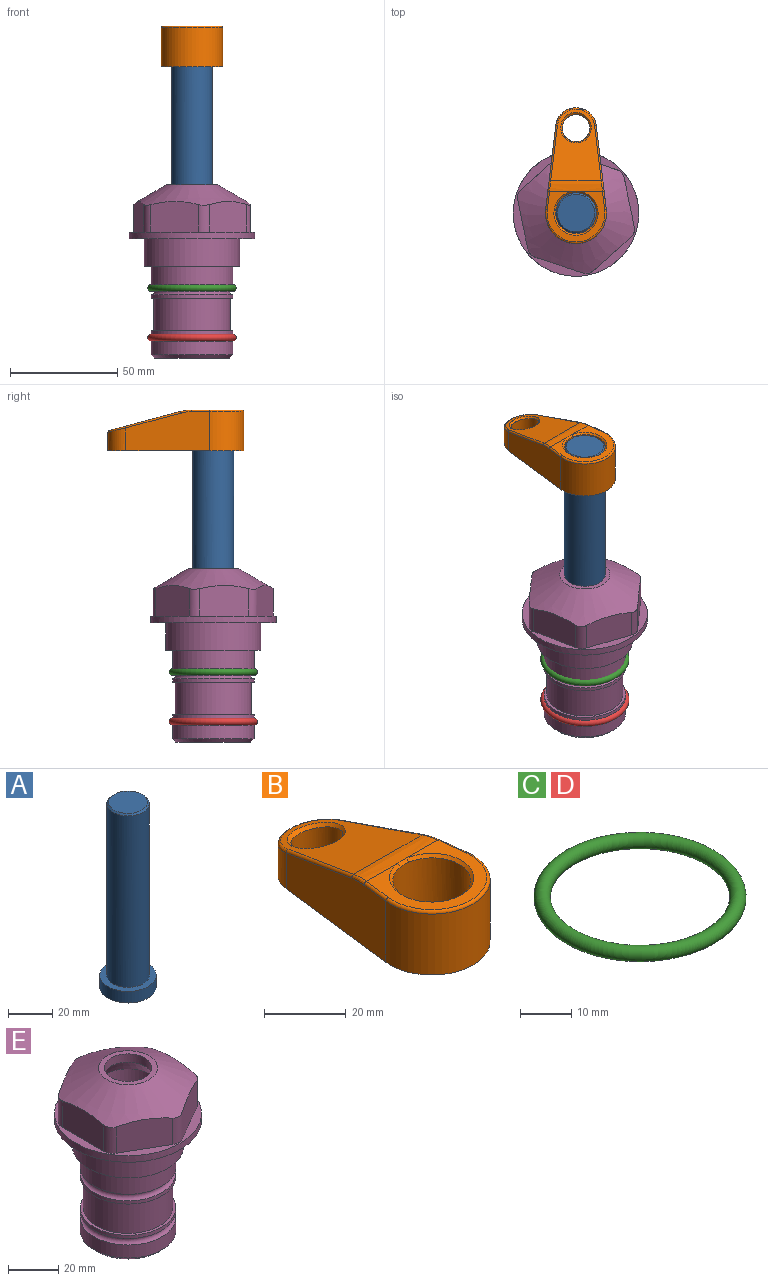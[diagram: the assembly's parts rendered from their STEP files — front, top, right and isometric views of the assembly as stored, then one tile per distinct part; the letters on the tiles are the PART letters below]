
ASSEMBLY  parts=5 mates=4
PART A: 6 faces, bbox 25.4x25.4x101.6 mm
  f0: plane 17.46x17.46mm, normal (0,0,1), area 239.5mm2, adj f5
  f1: plane 25.4x25.4mm, normal (0,0,-1), area 506.7mm2, adj f2
  f2: cylinder r=12.7mm len=25.4mm, axis (0,0,1), area 506.7mm2, adj f1,f3
  f3: plane 25.4x25.4mm, normal (0,0,1), area 221.7mm2, adj f2,f4
  f4: cylinder r=9.53mm len=94.46mm, axis (0,0,1), area 5653mm2, adj f3,f5
  f5: cone r=8.73mm half-angle=45deg, axis (0,0,-1), area 64.4mm2, adj f0,f4
PART B: 31 faces, bbox 31.7x65.5x19.8 mm
  f0: plane 39.12x18.26mm, normal (0.99,0.12,0), area 612.2mm2, adj f1,f4,f7,f11,f13,f15
  f1: cylinder r=9.53mm len=18.91mm, axis (0,0,-1), area 296.1mm2, adj f0,f2,f7,f17
  f2: plane 39.12x18.26mm, normal (-0.99,0.12,0), area 612.2mm2, adj f1,f4,f7,f12,f14,f16
  f3: cylinder r=6.35mm len=12.7mm, axis (0,0,-1), area 362.4mm2, adj f7,f18
  f4: cylinder r=14.29mm len=28.58mm, axis (0,0,-1), area 882.2mm2, adj f0,f2,f7,f10
  f5: cylinder r=9.53mm len=19.05mm, axis (0,0,-1), area 1092.6mm2, adj f7,f19,f20
  f6: plane 26.99x23.69mm, normal (0,0,1), area 216.2mm2, adj f9,f10,f11,f12,f19
  f7: plane 63.5x28.58mm, normal (0,0,-1), area 661.8mm2, adj f0,f1,f2,f3,f4,f5,f22,f23
  f8: plane 33.52x23.6mm, normal (0,0.26,0.97), area 486mm2, adj f9,f15,f16,f17,f18
  f9: cylinder r=19.05mm len=24.72mm, axis (1,0,0), area 120.4mm2, adj f6,f8,f13,f14,f20
  f10: torus R=13.49mm, axis (0,0,1), area 59mm2, adj f4,f6,f11,f12
  f11: cylinder r=0.79mm len=8.67mm, axis (0.12,-0.99,0), area 10.8mm2, adj f0,f6,f10,f13
  f12: cylinder r=0.79mm len=8.67mm, axis (0.12,0.99,0), area 10.8mm2, adj f2,f6,f10,f14
  f13: bspline ~4.95x1.42mm, area 6.1mm2, adj f0,f9,f11,f15
  f14: bspline ~4.95x1.42mm, area 6.1mm2, adj f2,f9,f12,f16
  f15: cylinder r=0.79mm len=25.95mm, axis (0.12,-0.96,0.26), area 32.9mm2, adj f0,f8,f13,f17
  f16: cylinder r=0.79mm len=25.95mm, axis (0.12,0.96,-0.26), area 32.9mm2, adj f2,f8,f14,f17
  f17: bspline ~18.91x8.38mm, area 30mm2, adj f1,f8,f15,f16
  f18: bspline ~14.29x14.29mm, area 48.3mm2, adj f3,f8
  f19: cone r=9.53mm half-angle=45deg, axis (0,0,1), area 66.5mm2, adj f5,f6,f20
  f20: bspline ~3.22x0.96mm, area 3.5mm2, adj f5,f9,f19
  f21: plane 2.75x2.72mm, normal (0,0,-1), area 2.9mm2, adj f23,f25,f28
  f22: plane 23.05x15.88mm, normal (-0.99,-0.12,0), area 323.6mm2, adj f7,f25,f26,f27,f28,f29
  f23: plane 23.05x15.88mm, normal (0.99,-0.12,0), area 323.6mm2, adj f7,f21,f25,f27,f28,f30
  f24: cylinder r=9.53mm len=10.69mm, axis (0,0,-1), area 114.7mm2, adj f7,f27,f29,f30
  f25: cylinder r=12.7mm len=20.59mm, axis (0,0,-1), area 381.1mm2, adj f7,f21,f22,f23,f26,f28
  f26: plane 2.75x2.72mm, normal (0,0,-1), area 2.9mm2, adj f22,f25,f28
  f27: plane 19.72x18.37mm, normal (0,-0.26,-0.97), area 291.8mm2, adj f22,f23,f24,f28,f29,f30
  f28: cylinder r=15.88mm len=19.92mm, axis (1,0,0), area 54.8mm2, adj f21,f22,f23,f25,f26,f27
  f29: cylinder r=1.59mm len=11mm, axis (0,0,-1), area 34.7mm2, adj f7,f22,f24,f27
  f30: cylinder r=1.59mm len=11mm, axis (0,0,-1), area 34.7mm2, adj f7,f23,f24,f27
PART C: 1 faces, bbox 44.7x44.7x3.2 mm
  f0: torus R=19.05mm, axis (0,0,1), area 1193.9mm2
PART D: same geometry as C
PART E: 36 faces, bbox 58.7x58.7x81 mm
  f0: cylinder r=17.78mm len=35.56mm, axis (0,0,1), area 1670.8mm2, adj f23,f24,f31
  f1: cylinder r=19.05mm len=38.1mm, axis (0,0,1), area 1191.9mm2, adj f26,f27,f30
  f2: plane 58.66x58.66mm, normal (0,0,-1), area 1150.6mm2, adj f3,f28
  f3: cylinder r=29.33mm len=58.66mm, axis (0,0,-1), area 585.1mm2, adj f2,f4
  f4: plane 58.66x58.66mm, normal (0,0,1), area 475.9mm2, adj f3,f5,f6,f7,f8,f9,f10,f11
  f5: plane 20.32x14.34mm, normal (-0.5,0.87,0), area 324.4mm2, adj f4,f15,f16,f17
  f6: plane 20.32x14.34mm, normal (0.5,0.87,0), area 324.4mm2, adj f4,f14,f15,f17
  f7: plane 23.48x14.34mm, normal (1,0,0), area 324.4mm2, adj f4,f13,f14,f17
  f8: plane 20.32x14.34mm, normal (0.5,-0.87,0), area 324.4mm2, adj f4,f12,f13,f17
  f9: plane 20.32x14.34mm, normal (-0.5,-0.87,0), area 324.4mm2, adj f4,f11,f12,f17
  f10: plane 23.48x14.34mm, normal (-1,0,0), area 324.4mm2, adj f4,f11,f16,f17
  f11: cylinder r=5.08mm len=12.85mm, axis (0,0,-1), area 67.2mm2, adj f4,f9,f10,f17
  f12: cylinder r=5.08mm len=12.85mm, axis (0,0,-1), area 67.2mm2, adj f4,f8,f9,f17
  f13: cylinder r=5.08mm len=12.85mm, axis (0,0,-1), area 67.2mm2, adj f4,f7,f8,f17
  f14: cylinder r=5.08mm len=12.85mm, axis (0,0,-1), area 67.2mm2, adj f4,f6,f7,f17
  f15: cylinder r=5.08mm len=12.85mm, axis (0,0,-1), area 67.2mm2, adj f4,f5,f6,f17
  f16: cylinder r=5.08mm len=12.85mm, axis (0,0,-1), area 67.2mm2, adj f4,f5,f10,f17
  f17: cone r=11.73mm half-angle=60deg, axis (0,0,-1), area 2071.8mm2, adj f5,f6,f7,f8,f9,f10,f11,f12
  f18: plane 23.46x23.46mm, normal (0,0,1), area 147.4mm2, adj f17,f35
  f19: plane 34.93x34.93mm, normal (0,0,-1), area 958mm2, adj f29
  f20: cylinder r=19.05mm len=38.1mm, axis (0,0,1), area 760.1mm2, adj f21,f29
  f21: torus R=19.05mm, axis (0,0,1), area 565.3mm2, adj f20,f22
  f22: cylinder r=19.05mm len=38.1mm, axis (0,0,1), area 190mm2, adj f21,f23
  f23: plane 38.1x38.1mm, normal (0,0,1), area 146.9mm2, adj f0,f22
  f24: plane 38.1x38.1mm, normal (0,0,-1), area 146.9mm2, adj f0,f25
  f25: cylinder r=19.05mm len=38.1mm, axis (0,0,1), area 190mm2, adj f24,f26
  f26: torus R=19.05mm, axis (0,0,1), area 565.3mm2, adj f1,f25
  f27: plane 44.45x44.45mm, normal (0,0,-1), area 411.7mm2, adj f1,f28
  f28: cylinder r=22.23mm len=44.45mm, axis (0,0,1), area 1773.5mm2, adj f2,f27
  f29: cone r=19.05mm half-angle=45deg, axis (0,0,1), area 257.5mm2, adj f19,f20
  f30: cylinder r=3.17mm len=6.75mm, axis (-1,0,0), area 128mm2, adj f1,f33
  f31: cylinder r=3.17mm len=6.35mm, axis (-1,0,0), area 102.5mm2, adj f0,f33
  f32: plane 25.4x25.4mm, normal (0,0,1), area 506.7mm2, adj f33
  f33: cylinder r=12.7mm len=66.42mm, axis (0,0,-1), area 5236.2mm2, adj f30,f31,f32,f34
  f34: cone r=9.53mm half-angle=30deg, axis (0,0,-1), area 443.4mm2, adj f33,f35
  f35: cylinder r=9.53mm len=19.05mm, axis (0,0,-1), area 240.9mm2, adj f18,f34
PLACE A at identity fixed
PLACE B t=(0,0,0.79)mm
PLACE C rot(axis=(0,0,1),71.5deg) t=(0,0,-33.59)mm
PLACE D rot(axis=(0,0,1),71.5deg) t=(0,0,-56.76)mm
PLACE E rot(axis=(0,0,1),71.5deg) t=(0,0,-35.17)mm
MATE fastened A.f2 <-> B.f4  axis (0,0,1) through (0,0,63.5)mm
MATE cylindrical E.f0 <-> A.f2  axis (0,0,1) through (0,0,-78.1)mm
MATE fastened E.f0 <-> C.f0  axis (0,0,1) through (0,0,-58.1)mm
MATE fastened E.f0 <-> D.f0  axis (0,0,1) through (0,0,-81.28)mm
